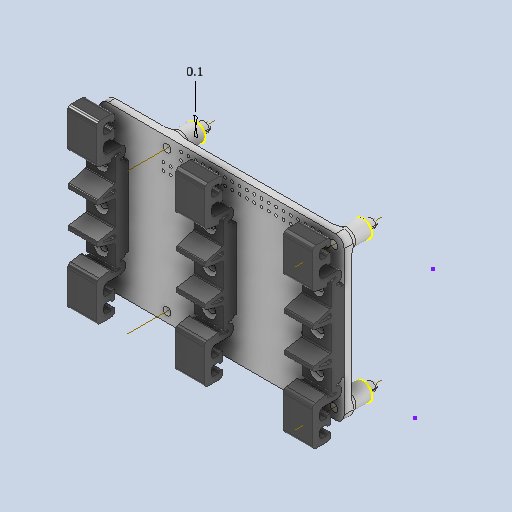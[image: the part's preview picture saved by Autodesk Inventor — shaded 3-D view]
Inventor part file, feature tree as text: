
AUTODESK INVENTOR PART (.ipt)
format: ipt  version: 2023 (Build 270158030, 158C)  size: 1,205,248 bytes
history: native  units: mm
features: other x23, reference x14, extrude x9, sketch x6, fillet x2, pattern_linear x2, chamfer x1, projected_geometry x1
ambient origin geometry x8: Origin, YZ Plane, XZ Plane, XY Plane, X Axis, Y Axis, Z Axis, Center Point
bodies: Solid4 (feature_tree), Solid5 (feature_tree)
feature tree (58):
  other  "backplate"
  other  "Blocks"
  extrude  "Extrusion1"  Depth=10.0mm TaperAngle=0.0deg
  extrude  "Extrusion2"  Depth=10.0mm TaperAngle=0.0deg
  extrude  "Extrusion3"  Depth=2.0mm TaperAngle=0.0deg
  fillet  "Fillet4"  Radius=4.0mm
  extrude  "Extrusion4"  Depth=2.5mm TaperAngle=0.0deg
  extrude  "Extrusion5"  Depth=1.759846mm
  other  "Work Axis10"
  other  "Work Axis11"
  other  "Work Axis12"
  other  "Work Axis13"
  extrude  "Extrusion6"  Depth=2.0mm
  fillet  "Fillet6"  Radius=0.1mm
  extrude  "Extrusion8"  Depth=2.0mm
  chamfer  "Chamfer1"  Distance=0.5mm
  extrude  "Extrusion9"  Depth=2.0mm
  extrude  "Extrusion10"  Depth=2.0mm
  pattern_linear  "Rectangular Pattern1"  Spacing1=3.44912mm  [1 undecoded]
  pattern_linear  "Rectangular Pattern2"  Spacing1=5.0mm  [1 undecoded]
  sketch  "Sketch1"  dims[d0=6.2mm d2=10.0mm d3=0.0mm]
  reference  "Reference2"
  sketch  "Sketch2"  dims[d4=2.5mm d5=0.0mm d9=10.0mm d10=0.0mm]
  other  "din-rail-clip-outline"
  projected_geometry  "Projected Loop1"
  sketch  "Sketch6"  dims[d12=2.0mm d16=2.0mm d17=0.0mm d18=4.0mm d19=0.785398mm]
  other  "crosscut"
  other  "Block3"
  reference  "Reference8"
  reference  "Reference9"
  reference  "Reference10"
  reference  "Reference11"
  reference  "Reference12"
  reference  "Reference13"
  reference  "Reference14"
  reference  "Reference15"
  reference  "Reference16"
  reference  "Reference17"
  reference  "Reference18"
  reference  "Reference19"
  reference  "Reference20"
  other  "DIN-rail-clip-long"
  sketch  "Sketch8"  dims[d21=0.4mm d25=2.5mm d26=0.0mm]
  sketch  "Sketch9"  dims[d27=1.0mm d30=1.759846mm]
  sketch  "Sketch10"  dims[d31=1.271846mm d32=3.0mm d40=0.1mm d41=0.2mm d42=0.5mm d43=3.1mm d44=3.4mm d46=3.44912mm d47=5.0mm d48=5.0mm d50=6.850895mm d51=6.850895mm d52=13.701789mm d53=0.0mm d54=0.0mm d55=1.0mm d56=2.0mm d57=45.0deg d58=0.0mm d59=0.0mm d60=5.47mm d61=2.0mm d62=0.0mm d63=30.0mm d65=75.0mm d66=30.0mm d68=75.0mm d69=2.0mm d70=2.0mm d74=2.6192mm d75=4.0mm d77=4.0mm d78=0.75mm d79=1.5mm d80=2.0mm d82=1.0mm d28=0.5mm d29=0.872665mm]
  other  "Pattern of DIN-rail-clip-long:1"
  other  "Pattern of DIN-rail-clip-long:2"
  other  "arduino-DIN-mount.iam"
  other  "arduinoMegaDetailed:1"
  other  "crosscut:1"
  other  "crosscut:2"
  other  "crosscut:3"
  other  "crosscut:5"
  other  "Block3:1"
  other  "raspi-DIN-mount.iam"
  other  "Raspberry Pi 4 Model B:1"
  other  "PCB, RPi4ModelB_1"
  other  "Block3:2"
note: 2 required parameter values undecoded (feature->parameter linkage not recoverable at this tier; creation-order binding heuristic only, values carry confidence <= 0.55)
